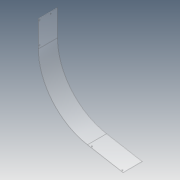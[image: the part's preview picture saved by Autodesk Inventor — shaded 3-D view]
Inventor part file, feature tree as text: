
AUTODESK INVENTOR PART (.ipt)
format: ipt  version: 2012 (Build 160160000, 160)  size: 95,232 bytes
history: native  units: in
note: dims shown in document units (in); Inventor stores cm internally (conversion verified against a paired STEP export)
features: pattern_linear x3, hole x2, extrude x1, sketch x1, reference x1
ambient origin geometry x8: Origin, YZ Plane, XZ Plane, XY Plane, X Axis, Y Axis, Z Axis, Center Point
bodies: Solid1 (feature_tree)
feature tree (8):
  extrude  "Extrusion1"  Depth=0.7874in
  hole  "Hole1"  [1 undecoded]
  pattern_linear  "Rectangular Pattern1"  Spacing1=0.5in  [1 undecoded]
  pattern_linear  "Rectangular Pattern2"  Count1=2 Spacing1=7.5in
  hole  "Hole2"  [1 undecoded]
  pattern_linear  "Rectangular Pattern4"  [2 undecoded]
  sketch  "Sketch1"  dims[d0=4.625in d1=0.0in d2=0.5in d3=0.3125in d4=0.265in d5=0.75in d6=0.375in d7=0.25in d8=0.5635in d9=1.0in d10=0.8108in d11=0.7874in d13=2.6875in d14=0.7874in d16=5.25in d17=0.5in d18=0.3125in d19=0.265in d20=0.75in d21=0.375in d22=0.25in d23=0.5635in d24=1.0in d25=0.8108in d29=0.7874in d31=7.5in]
  reference  "Reference1"
note: 5 required parameter values undecoded (feature->parameter linkage not recoverable at this tier; creation-order binding heuristic only, values carry confidence <= 0.55)
